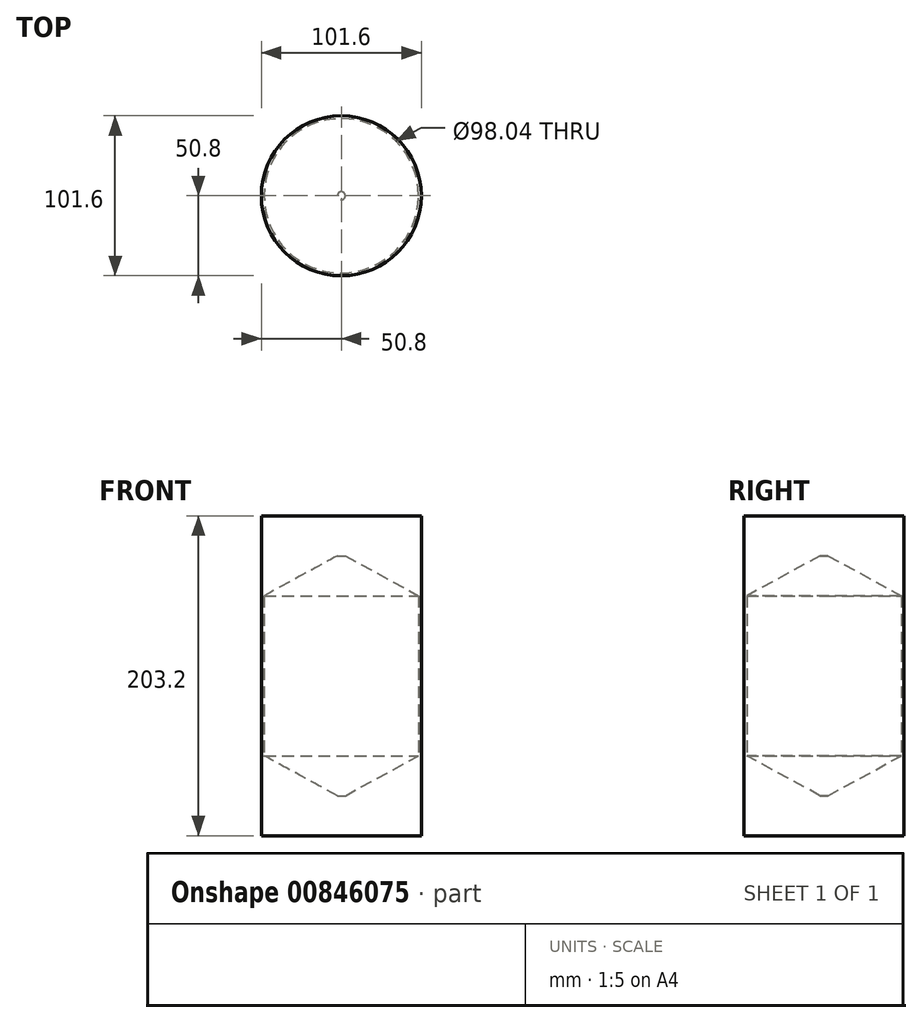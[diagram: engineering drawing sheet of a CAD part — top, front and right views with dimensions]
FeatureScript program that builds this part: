
annotation { "Feature Type Name" : "Feature", "Feature Type Description" : "" }
export const myFeature = defineFeature(function(context is Context, id is Id, definition is map)
    precondition{}
    {
        {
            var Q0;
            Q0=qCreatedBy(makeId("Front.planeOp"),FACE);
            var sketch = newSketch(context, id + "F0", { "sketchPlane" : qUnion([Q0])});
            skLineSegment(sketch, "E0.bottom", {"start": v(-50.8, 101.6) * mm, "end": v(50.8, 101.6) * mm});
            skLineSegment(sketch, "E0.top", {"start": v(-50.8, -101.6) * mm, "end": v(50.8, -101.6) * mm});
            skLineSegment(sketch, "E0.left", {"start": v(-50.8, 101.6) * mm, "end": v(-50.8, -101.6) * mm});
            skLineSegment(sketch, "E0.right", {"start": v(50.8, 101.6) * mm, "end": v(50.8, -101.6) * mm});
            skPoint(sketch, "E0.middle", {"position": v(0, 0) * mm});
            skLineSegment(sketch, "E1.bottom", {"start": v(-2.54, 76.2) * mm, "end": v(2.54, 76.2) * mm});
            skLineSegment(sketch, "E1.top", {"start": v(-2.54, -76.2) * mm, "end": v(2.54, -76.2) * mm});
            skLineSegment(sketch, "E1.left", {"start": v(-49.02, 50.8) * mm, "end": v(-49.02, -50.8) * mm});
            skLineSegment(sketch, "E1.right", {"start": v(49.02, 50.8) * mm, "end": v(49.02, -50.8) * mm});
            skLineSegment(sketch, "E2", {"start": v(0, -101.6) * mm, "end": v(0, 101.6) * mm});
            skLineSegment(sketch, "E3", {"start": v(-2.54, 76.2) * mm, "end": v(-49.02, 50.8) * mm});
            skLineSegment(sketch, "E4", {"start": v(2.54, 76.2) * mm, "end": v(49.02, 50.8) * mm});
            skLineSegment(sketch, "E5", {"start": v(-49.02, -50.8) * mm, "end": v(-2.54, -76.2) * mm});
            skLineSegment(sketch, "E6", {"start": v(49.02, -50.8) * mm, "end": v(2.54, -76.2) * mm});
            skSolve(sketch);
        }
        {
            var Q0;
            {var subQ4=sQuery(id+"F0.wireOp",EDGE,"E0.left");Q0=makeQuery(id+"F0.imprint","IMPRINT",FACE,{"disambiguationData":[TD([[makeQuery(id+"F0.imprint","IMPRINT",EDGE,{"derivedFrom":subQ4}),1.0]])]});}
            var Q1;
            Q1=sQuery(id+"F0.wireOp",EDGE,"E2");
            revolve(context, id + "F1", {"surfaceOperationType" : NewSurfaceOperationType.NEW, "entities" : qUnion([Q0]), "axis" : qUnion([Q1]), "revolveType" : RevolveType.FULL});
        }
    });
